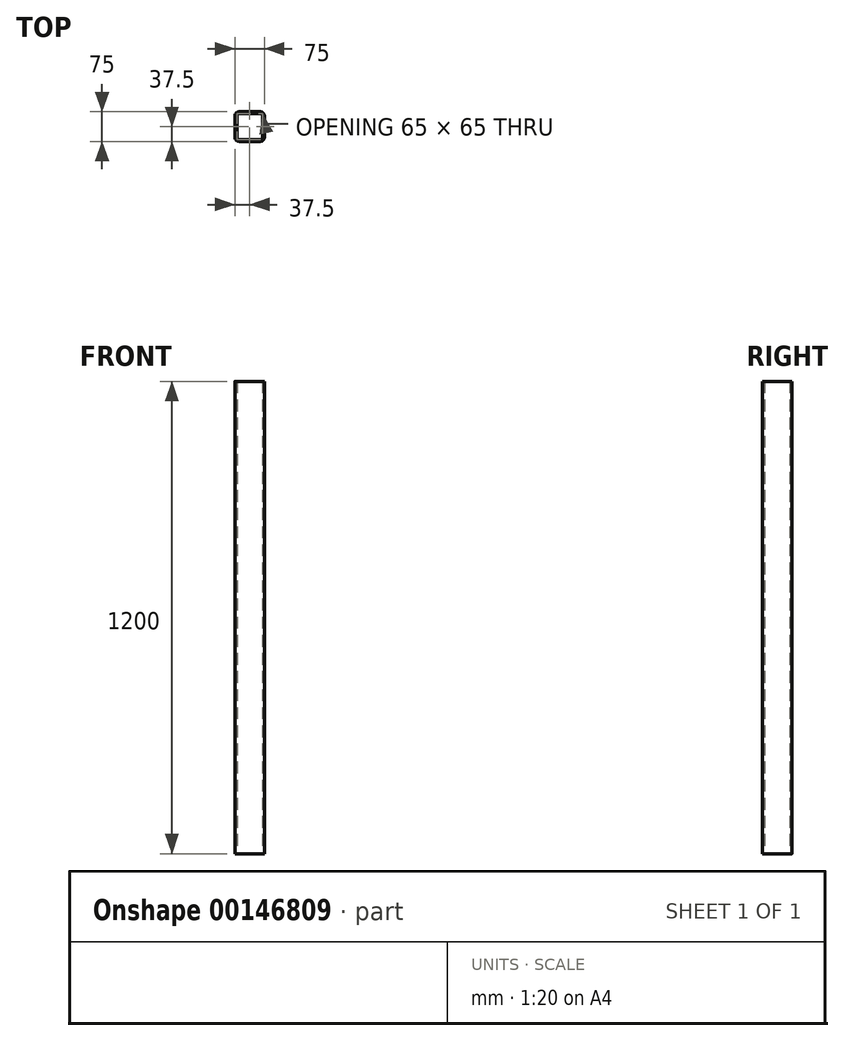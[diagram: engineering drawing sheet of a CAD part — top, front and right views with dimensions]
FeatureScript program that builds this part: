
annotation { "Feature Type Name" : "Feature", "Feature Type Description" : "" }
export const myFeature = defineFeature(function(context is Context, id is Id, definition is map)
    precondition{}
    {
        {
            var Q0;
            Q0=qCreatedBy(makeId("Top.planeOp"),FACE);
            var sketch = newSketch(context, id + "F0", { "sketchPlane" : qUnion([Q0])});
            skLineSegment(sketch, "E0.bottom", {"start": v(27.5, 37.5) * mm, "end": v(-27.5, 37.5) * mm});
            skLineSegment(sketch, "E0.top", {"start": v(27.5, -37.5) * mm, "end": v(-27.5, -37.5) * mm});
            skLineSegment(sketch, "E0.left", {"start": v(37.5, 27.5) * mm, "end": v(37.5, -27.5) * mm});
            skLineSegment(sketch, "E0.right", {"start": v(-37.5, 27.5) * mm, "end": v(-37.5, -27.5) * mm});
            skPoint(sketch, "E0.middle", {"position": v(0, 0) * mm});
            skPoint(sketch, "E1.visualSharp", {"position": v(-37.5, 37.5) * mm});
            skArc(sketch, "E1.filletArc", {"start": v(-27.5, 37.5) * mm, "mid": v(-34.57, 34.57) * mm, "end": v(-37.5, 27.5) * mm});
            skPoint(sketch, "E2.visualSharp", {"position": v(37.5, 37.5) * mm});
            skArc(sketch, "E2.filletArc", {"start": v(37.5, 27.5) * mm, "mid": v(34.57, 34.57) * mm, "end": v(27.5, 37.5) * mm});
            skPoint(sketch, "E3.visualSharp", {"position": v(37.5, -37.5) * mm});
            skArc(sketch, "E3.filletArc", {"start": v(27.5, -37.5) * mm, "mid": v(34.57, -34.57) * mm, "end": v(37.5, -27.5) * mm});
            skPoint(sketch, "E4.visualSharp", {"position": v(-37.5, -37.5) * mm});
            skArc(sketch, "E4.filletArc", {"start": v(-37.5, -27.5) * mm, "mid": v(-34.57, -34.57) * mm, "end": v(-27.5, -37.5) * mm});
            skArc(sketch, "E5.0", {"start": v(32.5, 27.5) * mm, "mid": v(31.04, 31.04) * mm, "end": v(27.5, 32.5) * mm});
            skLineSegment(sketch, "E5.1", {"start": v(32.5, 27.5) * mm, "end": v(32.5, -27.5) * mm});
            skLineSegment(sketch, "E5.2", {"start": v(27.5, 32.5) * mm, "end": v(-27.5, 32.5) * mm});
            skArc(sketch, "E5.3", {"start": v(27.5, -32.5) * mm, "mid": v(31.04, -31.04) * mm, "end": v(32.5, -27.5) * mm});
            skArc(sketch, "E5.4", {"start": v(-27.5, 32.5) * mm, "mid": v(-31.04, 31.04) * mm, "end": v(-32.5, 27.5) * mm});
            skLineSegment(sketch, "E5.5", {"start": v(-32.5, 27.5) * mm, "end": v(-32.5, -27.5) * mm});
            skArc(sketch, "E5.6", {"start": v(-32.5, -27.5) * mm, "mid": v(-31.04, -31.04) * mm, "end": v(-27.5, -32.5) * mm});
            skLineSegment(sketch, "E5.7", {"start": v(27.5, -32.5) * mm, "end": v(-27.5, -32.5) * mm});
            skSolve(sketch);
        }
        {
            var Q0;
            Q0=makeQuery(id+"F0.imprint","IMPRINT",FACE,{"disambiguationData":[TD([[makeQuery(id+"F0.imprint","IMPRINT",EDGE,{"derivedFrom":sQuery(id+"F0.wireOp",EDGE,"E0.bottom")}),1.0]])]});
            extrude(context, id + "F1", {"entities" : qUnion([Q0]), "depth" : 1200 * mm});
        }
    });
